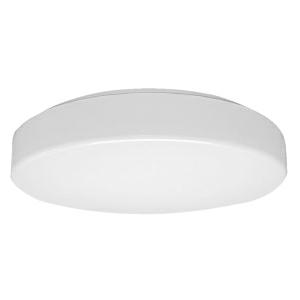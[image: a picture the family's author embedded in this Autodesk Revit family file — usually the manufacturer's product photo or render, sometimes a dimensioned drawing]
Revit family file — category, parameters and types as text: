
# Revit family: oblo_fit_-_oba_1000_840_d_00813347_699c
name_source: partatom
category: Lighting Fixtures
units: mm (PartAtom-declared; Revit-internal decimal feet)

## family parameters
Cut with Voids When Loaded = No
Host = Face
Light Source = No
Part Type = Normal
Room Calculation Point = No
Round Connector Dimension = Use Diameter
Shared = No

## types (1)
- OBLO.fit - OBA 1000/840/D (1 x LED, 1500 lm, 4000K)
    Apparent Load = 11 VA
    Approval mark = CE
    CIE Flux Codes = 41 72 91 84 100
    Color Rendering = 80-89
    Color Temperature = 4000K
    Control Gear = Electronic ballast
    Default Elevation = 1800 mm
    Description = OBA 1000/840/D|Surface-mounted luminaire.|light source:   Cold white   |work equipment: Power supply unit|luminous flux: 1500 lm|light distribution: Direct|class of protection: I|technology: Continuously dimmable|mains lead: Direct power supply|glare control: without|special features: DALI Load 1x|
    Frequency = 50 Hz, 60 Hz
    Height = 85 mm
    Lamp = 1 x LED
    Lamp Light Flux = 1500 lm
    Lamp count = 1
    Length = 300 mm
    Luminous efficacy = 136 lm/W
    Manufacturer = Waldmann
    ModVariant = No
    Model = 00813347
    Mounting Place = Ceiling
    Mounting Type = Surface mounted
    Number of Poles = 1
    OnlyDefault = Yes
    Power Factor = 1
    Product Name = OBLO.fit - OBA 1000/840/D
    Product group = Ceiling mounted luminaire
    ProductGroupID = 3
    Protection Class = Protection class I
    Protection Degree = IP 40
    RLX_Detail_Level = 1
    RLX_Emergency_Light_Flux = 0 lm
    RLX_Emergency_Type = 0
    RLX_Emergency_Type_DB = No
    RlxData = <blob elided: 22289 chars, md5=7bee067a>
    Socket = socket
    Standby Power = 0 W
    System Light Flux = 1500 lm
    System Power = 11 W
    Type Comments = Product without accessories
    Type Image = oblo_led.jpg
    URL = http://relux.com
    VarID = ---
    Voltage = 230 V
    Voltage Range = 220-240 V
    Weight = 0.00 kg
    Width = 0 mm  [stored 0 ft]

note: [stored X ft] marks values corroborated as IEEE doubles in the binary element streams (Revit-internal decimal feet)

## geometry (parser evidence)
native form markers: Blend x4, Sweep x13
no freeform markers — native parametric forms only
